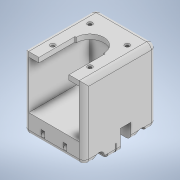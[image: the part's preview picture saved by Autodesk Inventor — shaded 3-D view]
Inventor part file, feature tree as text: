
AUTODESK INVENTOR PART (.ipt)
format: ipt  version: 2022.3 (Build 263350000, 350)  size: 650,752 bytes
history: native  units: mm
features: extrude x12, sketch x10, thicken_offset x10, fillet x3, hole x1, projected_geometry x1
ambient origin geometry x8: Origin, YZ Plane, XZ Plane, XY Plane, X Axis, Y Axis, Z Axis, Center Point
bodies: Solid1 (feature_tree)
feature tree (37):
  extrude  "Extrusion1"  Depth=60.0mm
  extrude  "Extrusion2"  Depth=4.0mm
  sketch  "Sketch3"  dims[d5=25.0mm d6=8.0mm]
  extrude  "Extrusion3"  Depth=8.0mm
  extrude  "Extrusion4"  Depth=42.0mm
  fillet  "Fillet1"  Radius=51.0mm
  extrude  "Extrusion5"  Depth=35.0mm
  hole  "Hole1"  [1 undecoded]
  extrude  "Extrusion6"  Depth=13.0mm TaperAngle=0.0deg
  thicken_offset  "Thicken1"
  thicken_offset  "Thicken2"
  thicken_offset  "Thicken3"
  thicken_offset  "Thicken4"
  thicken_offset  "Thicken5"
  thicken_offset  "Thicken6"
  extrude  "Extrusion7"  Depth=4.0mm
  fillet  "Fillet2"  Radius=22.0mm
  extrude  "Extrusion8"  Depth=42.0mm
  sketch  "Sketch9"  dims[d22=0.0mm d23=0.0mm d24=42.0mm]
  extrude  "Extrusion9"  Depth=4.0mm
  fillet  "Fillet3"  Radius=31.0mm
  extrude  "Extrusion11"  Depth=4.0mm
  extrude  "Extrusion12"  Depth=4.0mm
  thicken_offset  "Thicken8"
  thicken_offset  "Thicken9"
  thicken_offset  "Thicken10"
  thicken_offset  "Thicken11"
  extrude  "Extrusion13"  Depth=4.0mm TaperAngle=0.0deg
  sketch  "Sketch1"  dims[d0=50.0mm d1=60.0mm]
  sketch  "Sketch2"  dims[d2=60.5mm d3=0.0mm d4=4.0mm]
  sketch  "Sketch4"  dims[d7=45.0mm d8=42.0mm d9=51.0mm d10=0.0mm]
  sketch  "Sketch5"  dims[d11=17.5mm d12=35.0mm]
  sketch  "Sketch6"  dims[d13=15.0mm d14=15.0mm]
  sketch  "Sketch7"  dims[d15=37.0mm d16=0.0mm d17=13.0mm d18=0.0mm]
  sketch  "Sketch8"  dims[d19=4.0mm d20=18.0mm d21=22.0mm]
  sketch  "Sketch10"  dims[d25=90.0deg d26=31.0mm d27=31.0mm d28=2.4mm d29=6.0mm d30=4.0mm d31=2.0mm d32=90.0deg d33=4.0mm d34=0.0mm d35=9.0mm d36=9.0mm d37=37.0mm d38=0.0mm d39=1.0mm d40=1.0mm d41=1.0mm d42=1.0mm d43=1.0mm d44=1.0mm d45=1.0mm d46=1.0mm d47=5.0mm d48=5.0mm d49=2.0mm d50=2.0mm d51=5.3mm d52=5.3mm d53=3.0mm d54=3.0mm d55=2.0mm d56=2.0mm d57=0.0mm d58=0.0mm d59=3.0mm d60=23.0mm d61=60.5mm d62=0.0mm d63=5.0mm d64=5.0mm d65=4.5mm d66=50.0mm d67=3.0mm d68=1.0mm d69=0.75mm d70=7.0mm d71=0.75mm d72=1.0mm d73=1.0mm d74=1.0mm d75=0.75mm d76=1.0mm d77=0.75mm d78=1.0mm d79=1.0mm d80=0.75mm d81=0.75mm d82=1.0mm d83=0.75mm d84=110.0mm d86=2.0mm d87=10.0mm d89=10.0mm d91=10.0mm d93=10.0mm d94=110.0mm d96=2.0mm d98=10.0mm d99=0.0mm d100=4.0mm d106=3.0mm d107=3.0mm d108=3.5mm d109=0.0mm d110=3.5mm d111=0.0mm d112=4.0mm d113=2.0mm d114=4.0mm d115=2.0mm d116=4.0mm d117=2.0mm d118=4.0mm d119=2.0mm d120=0.0mm d121=0.0mm]
  projected_geometry  "Projected Loop1"
note: 1 required parameter value undecoded (feature->parameter linkage not recoverable at this tier; creation-order binding heuristic only, values carry confidence <= 0.55)
